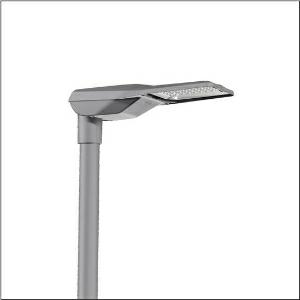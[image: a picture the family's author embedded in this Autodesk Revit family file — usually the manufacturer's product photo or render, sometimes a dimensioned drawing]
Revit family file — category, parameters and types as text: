
# Revit family: streetlight_sl_21_iq_mini___st0_5a_5xe2b41d08jb_1bd7
name_source: partatom
category: Lighting Fixtures
units: mm (PartAtom-declared; Revit-internal decimal feet)

## family parameters
Cut with Voids When Loaded = No
Host = Face
Light Source = No
Part Type = Normal
Room Calculation Point = No
Round Connector Dimension = Use Diameter
Shared = No

## types (1)
- --- (1 x LED, 11290 lm, 71.6 W, 4000K)
    Apparent Load = 72 VA
    CIE Flux Codes = 43 76 97 100 100
    Color Rendering = 70
    Color Temperature = 4000K
    Default Elevation = 1800 mm
    Description = Streetlight SL 21 iQ mini, mast luminaire, primary light control with lens, of PMMA, primary optical cover: cover, of toughened safety glass, transparent, light distribution: ST0.5a, light emission: direct distribution, primary light characteristic: asymmetric, installation type: post-top, side-entry, LED, High Power LED, rated luminous flux: 11.290lm, luminous efficacy: 158lm/W, light colour: 740, colour temperature: 4000K, control gear: iQ-Comfort, control: Auto-Match, Temp-Guard, Lumen-Switch, Night-Set, Smart-Wire, Light-Fading, Desk-Remote (wireless, voltage-free reading and setting of iQ features in the workshop via application-optimized NFC function/RFID function), optimised constant luminous flux control (CLO 2.0), pre-setting: linear dimming characteristic, mains connection: 220..240V, AC, 50/60Hz, start of lifetime: 72W, end of service life: 75W, reduction: 33W, luminaire housing, of diecast aluminium, powder-coated, SITECO metallic grey (DB 702S), corrosivity category C5 high according to DIN EN ISO 12944, please order mast flange separately, inclination adjustable: 0°, 5°, 10°, 15°, sealing non-destructively replaceable, multi-level sealing system, length: 628mm, width: 235mm, height: 110mm, mast flange for spigot size: 42mm (side-entry): 5XC10008XM4, 60/48mm (side-entry/post-top): 5XC10108XM2, 76/60mm (side-entry/post-top): 5XC10108XM1, mounting height: 4..8m, protection rating (complete): IP66, insulation class (complete): insulation class II (safety insulation), certification: CE, ENEC, ENEC+, VDE, impact resistance: IK10, permissible operating ambient temperature for outdoor applications: -40..+50°C, standard-compliant lighting for roads and squares, packaging unit: 1 piece

Light Distribution: ST0.5a
    Height = 110 mm
    Lamp = 1 x LED
    Lamp Light Flux = 11290 lm
    Lamp Power = 71.6 W
    Lamp count = 1
    Length = 625 mm
    Luminous efficacy = 158 lm/W
    Manufacturer = Siteco
    ModVariant = No
    Model = 5XE2B41D08JB
    Number of Poles = 1
    OnlyDefault = Yes
    Power Factor = 1
    Product Name = Streetlight SL 21 iQ mini | ST0.5a
    Product group = mast luminaire | pylon top
    ProductGroupID = 6100
    Protection Class = Protection class II
    Protection Degree = IP 66
    RLX_Detail_Level = 1
    RLX_Emergency_Light_Flux = 0 lm
    RLX_Emergency_Type = 0
    RLX_Emergency_Type_DB = No
    RlxData = <blob elided: 37581 chars, md5=530bcc41>
    Socket = socket
    Standby Power = 0 W
    System Light Flux = 11290 lm
    System Power = 72 W
    Type Comments = factory setting: luminous flux: 100 % | dim-lin: 254 | 746 mA
    Type Image = l_1003519.jpg
    URL = http://relux.com
    VarID = @adj_171217
    Voltage = 0 V
    Weight = 0.00 kg
    Width = 234 mm

## geometry (parser evidence)
native form markers: Blend x4, Sweep x12
no freeform markers — native parametric forms only
